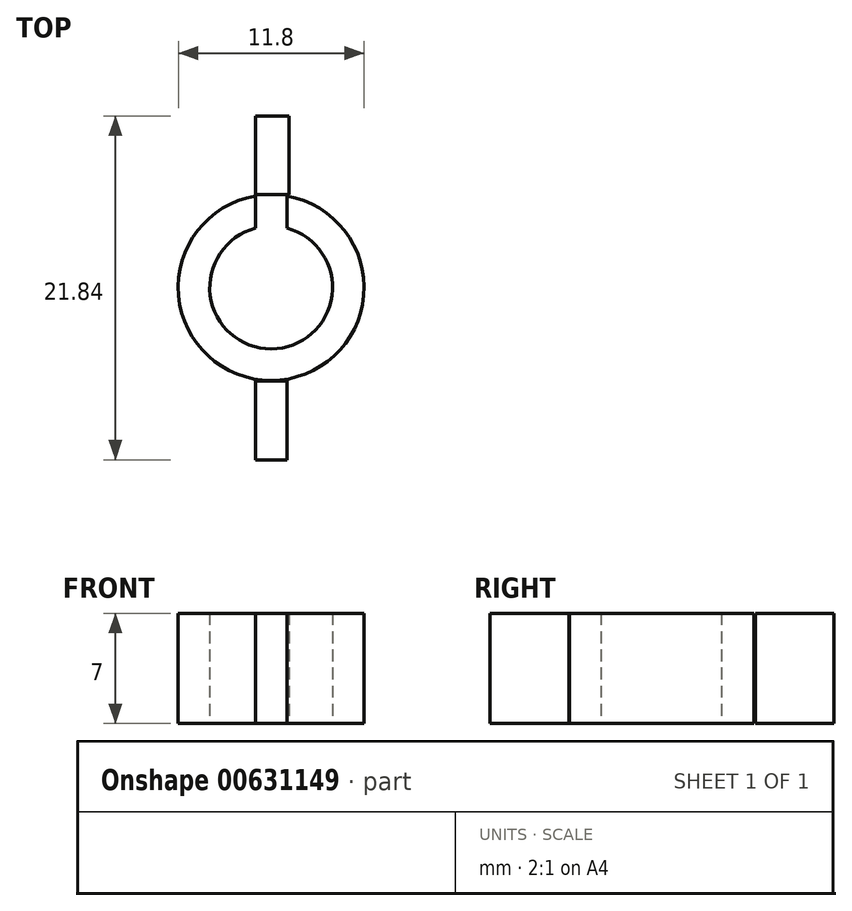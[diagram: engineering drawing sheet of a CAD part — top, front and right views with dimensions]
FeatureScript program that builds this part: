
annotation { "Feature Type Name" : "Feature", "Feature Type Description" : "" }
export const myFeature = defineFeature(function(context is Context, id is Id, definition is map)
    precondition{}
    {
        {
            var Q0;
            Q0=qCreatedBy(makeId("Top.planeOp"),FACE);
            var sketch = newSketch(context, id + "F0", { "sketchPlane" : qUnion([Q0])});
            skCircle(sketch, "E0", {"center": v(-50.38, 12.18) * mm, "radius": 3.9 * mm});
            skCircle(sketch, "E1.0", {"center": v(-50.38, 12.18) * mm, "radius": 5.9 * mm});
            skLineSegment(sketch, "E2", {"start": v(-50.38, 12.18) * mm, "end": v(-50.38, 18.08) * mm});
            skLineSegment(sketch, "E3", {"start": v(-50.38, 18.08) * mm, "end": v(-50.38, 6.28) * mm});
            skLineSegment(sketch, "E4.0", {"start": v(-49.38, 18.08) * mm, "end": v(-49.38, 6.28) * mm});
            skLineSegment(sketch, "E5.0", {"start": v(-51.38, 18.08) * mm, "end": v(-51.38, 6.24) * mm});
            skLineSegment(sketch, "E6.bottom", {"start": v(-51.38, 6.24) * mm, "end": v(-49.38, 6.24) * mm});
            skLineSegment(sketch, "E6.top", {"start": v(-51.38, 1.24) * mm, "end": v(-49.38, 1.24) * mm});
            skLineSegment(sketch, "E6.left", {"start": v(-51.38, 6.24) * mm, "end": v(-51.38, 1.24) * mm});
            skLineSegment(sketch, "E6.right", {"start": v(-49.38, 6.24) * mm, "end": v(-49.38, 1.24) * mm});
            skLineSegment(sketch, "E7.bottom", {"start": v(-51.38, 18.08) * mm, "end": v(-49.26, 18.08) * mm});
            skLineSegment(sketch, "E7.top", {"start": v(-51.38, 23.08) * mm, "end": v(-49.26, 23.08) * mm});
            skLineSegment(sketch, "E7.left", {"start": v(-51.38, 18.08) * mm, "end": v(-51.38, 23.08) * mm});
            skLineSegment(sketch, "E7.right", {"start": v(-49.26, 18.08) * mm, "end": v(-49.26, 23.08) * mm});
            skSolve(sketch);
        }
        {
            var Q0;
            {var subQ0=sQuery(id+"F0.wireOp",EDGE,"E5.0");var subQ1=sQuery(id+"F0.wireOp",EDGE,"E0");var subQ2=makeQuery(id+"F0.imprint","INTERSECT",VERTEX,{"disambiguationData":[OD(0.0)],"derivedFrom":[subQ1,subQ0]});Q0=makeQuery(id+"F0.imprint","IMPRINT",FACE,{"disambiguationData":[TD([[makeQuery(id+"F0.imprint","IMPRINT",EDGE,{"disambiguationData":[TD([[subQ2,-1.0]])],"derivedFrom":subQ1}),-1.0]])]});}
            var Q1;
            {var subQ0=sQuery(id+"F0.wireOp",EDGE,"E4.0");var subQ1=sQuery(id+"F0.wireOp",EDGE,"E0");var subQ2=makeQuery(id+"F0.imprint","INTERSECT",VERTEX,{"disambiguationData":[OD(0.0)],"derivedFrom":[subQ1,subQ0]});Q1=makeQuery(id+"F0.imprint","IMPRINT",FACE,{"disambiguationData":[TD([[makeQuery(id+"F0.imprint","IMPRINT",EDGE,{"disambiguationData":[TD([[subQ2,1.0]])],"derivedFrom":subQ1}),-1.0]])]});}
            var Q2;
            {var subQ0=sQuery(id+"F0.wireOp",EDGE,"E3");var subQ1=sQuery(id+"F0.wireOp",EDGE,"E0");var subQ2=makeQuery(id+"F0.imprint","INTERSECT",VERTEX,{"disambiguationData":[OD(0.0)],"derivedFrom":[subQ1,subQ0]});Q2=makeQuery(id+"F0.imprint","IMPRINT",FACE,{"disambiguationData":[TD([[makeQuery(id+"F0.imprint","IMPRINT",EDGE,{"disambiguationData":[TD([[subQ2,1.0]])],"derivedFrom":subQ1}),-1.0]])]});}
            var Q3;
            {var subQ0=sQuery(id+"F0.wireOp",EDGE,"E3");var subQ1=sQuery(id+"F0.wireOp",EDGE,"E0");var subQ2=makeQuery(id+"F0.imprint","INTERSECT",VERTEX,{"disambiguationData":[OD(0.0)],"derivedFrom":[subQ1,subQ0]});Q3=makeQuery(id+"F0.imprint","IMPRINT",FACE,{"disambiguationData":[TD([[makeQuery(id+"F0.imprint","IMPRINT",EDGE,{"disambiguationData":[TD([[subQ2,-1.0]])],"derivedFrom":subQ1}),-1.0]])]});}
            var Q4;
            Q4=makeQuery(id+"F0.imprint","IMPRINT",FACE,{"disambiguationData":[TD([[makeQuery(id+"F0.imprint","IMPRINT",EDGE,{"derivedFrom":sQuery(id+"F0.wireOp",EDGE,"E7.top")}),-1.0]])]});
            var Q5;
            {var subQ0=sQuery(id+"F0.wireOp",EDGE,"E5.0");var subQ1=sQuery(id+"F0.wireOp",EDGE,"E0");var subQ2=makeQuery(id+"F0.imprint","INTERSECT",VERTEX,{"disambiguationData":[OD(1.0)],"derivedFrom":[subQ1,subQ0]});Q5=makeQuery(id+"F0.imprint","IMPRINT",FACE,{"disambiguationData":[TD([[makeQuery(id+"F0.imprint","IMPRINT",EDGE,{"disambiguationData":[TD([[subQ2,-1.0]])],"derivedFrom":subQ1}),-1.0]])]});}
            var Q6;
            {var subQ0=sQuery(id+"F0.wireOp",EDGE,"E3");var subQ1=sQuery(id+"F0.wireOp",EDGE,"E0");var subQ2=makeQuery(id+"F0.imprint","INTERSECT",VERTEX,{"disambiguationData":[OD(1.0)],"derivedFrom":[subQ1,subQ0]});Q6=makeQuery(id+"F0.imprint","IMPRINT",FACE,{"disambiguationData":[TD([[makeQuery(id+"F0.imprint","IMPRINT",EDGE,{"disambiguationData":[TD([[subQ2,-1.0]])],"derivedFrom":subQ1}),-1.0]])]});}
            var Q7;
            Q7=makeQuery(id+"F0.imprint","IMPRINT",FACE,{"disambiguationData":[TD([[makeQuery(id+"F0.imprint","IMPRINT",EDGE,{"derivedFrom":sQuery(id+"F0.wireOp",EDGE,"E6.bottom")}),-1.0]])]});
            extrude(context, id + "F1", {"entities" : qUnion([Q0, Q1, Q2, Q3, Q4, Q5, Q6, Q7]), "depth" : 7 * mm, "offsetDistance" : 25 * mm});
        }
    });
